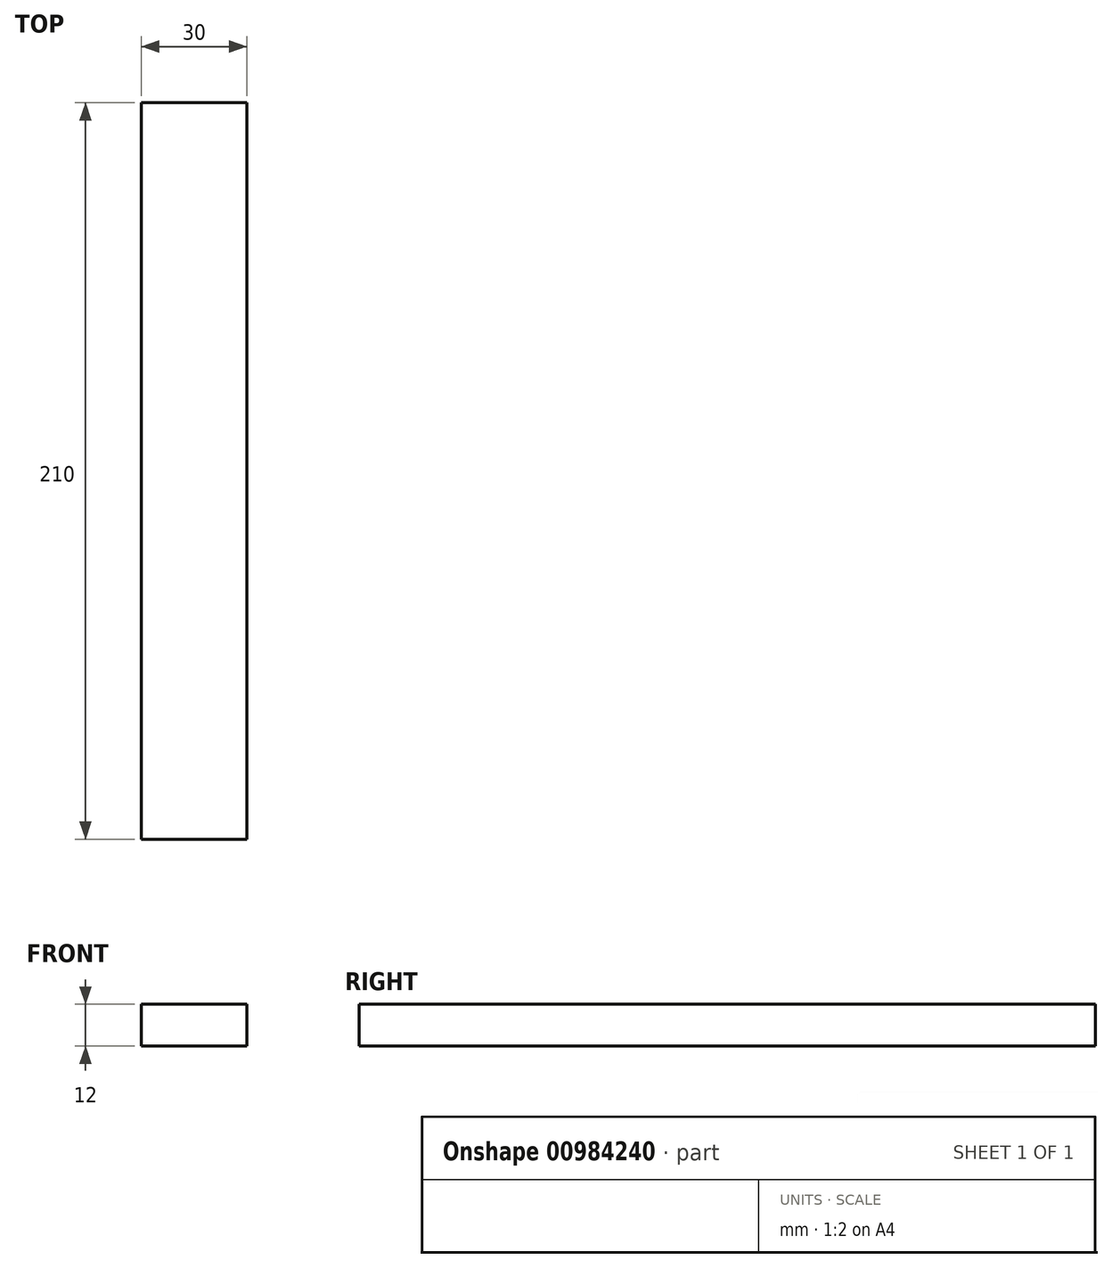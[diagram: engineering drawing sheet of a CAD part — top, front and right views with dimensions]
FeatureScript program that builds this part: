
annotation { "Feature Type Name" : "Feature", "Feature Type Description" : "" }
export const myFeature = defineFeature(function(context is Context, id is Id, definition is map)
    precondition{}
    {
        {
            var Q0;
            Q0=qCreatedBy(makeId("Top.planeOp"),FACE);
            var sketch = newSketch(context, id + "F0", { "sketchPlane" : qUnion([Q0])});
            skLineSegment(sketch, "E0.bottom", {"start": v(15, 105) * mm, "end": v(-15, 105) * mm});
            skLineSegment(sketch, "E0.top", {"start": v(15, -105) * mm, "end": v(-15, -105) * mm});
            skLineSegment(sketch, "E0.left", {"start": v(15, 105) * mm, "end": v(15, -105) * mm});
            skLineSegment(sketch, "E0.right", {"start": v(-15, 105) * mm, "end": v(-15, -105) * mm});
            skPoint(sketch, "E0.middle", {"position": v(0, 0) * mm});
            skSolve(sketch);
        }
        {
            var Q0;
            Q0=makeQuery(id+"F0.imprint","IMPRINT",FACE,{"disambiguationData":[TD([[makeQuery(id+"F0.imprint","IMPRINT",EDGE,{"derivedFrom":sQuery(id+"F0.wireOp",EDGE,"E0.bottom")}),1.0]])]});
            extrude(context, id + "F1", {"entities" : qUnion([Q0]), "oppositeDirection" : true, "depth" : 12 * mm, "offsetDistance" : 25 * mm});
        }
    });
